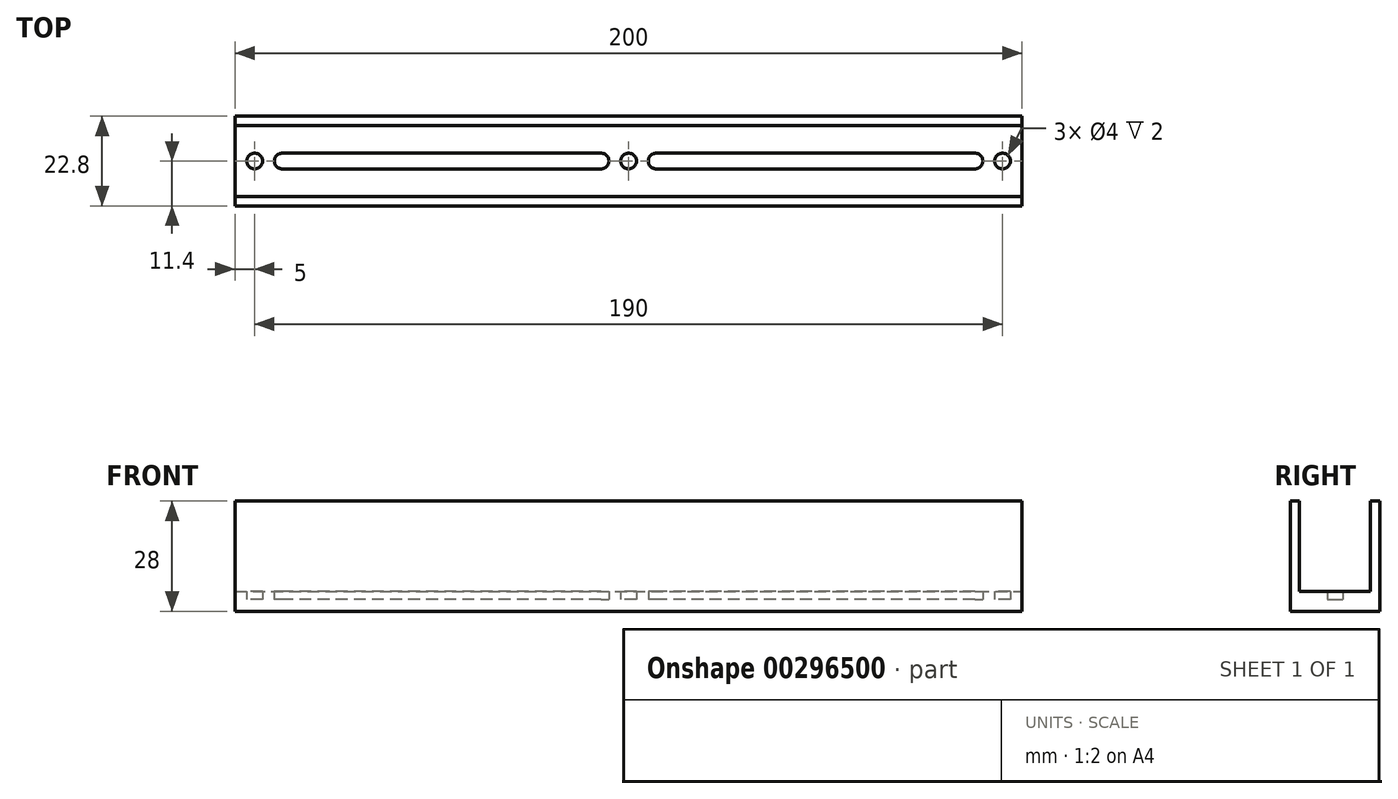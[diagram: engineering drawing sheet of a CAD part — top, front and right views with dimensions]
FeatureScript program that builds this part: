
annotation { "Feature Type Name" : "Feature", "Feature Type Description" : "" }
export const myFeature = defineFeature(function(context is Context, id is Id, definition is map)
    precondition{}
    {
        {
            var Q0;
            Q0=qCreatedBy(makeId("Top.planeOp"),FACE);
            var sketch = newSketch(context, id + "F0", { "sketchPlane" : qUnion([Q0])});
            skLineSegment(sketch, "E0.bottom", {"start": v(0, 0) * mm, "end": v(200, 0) * mm});
            skLineSegment(sketch, "E0.top", {"start": v(0, 18) * mm, "end": v(200, 18) * mm});
            skLineSegment(sketch, "E0.left", {"start": v(0, 0) * mm, "end": v(0, 18) * mm});
            skLineSegment(sketch, "E0.right", {"start": v(200, 0) * mm, "end": v(200, 18) * mm});
            skLineSegment(sketch, "E1", {"start": v(200, 9) * mm, "end": v(0, 9) * mm, "construction": true});
            skCircle(sketch, "E2", {"center": v(100, 9) * mm, "radius": 2 * mm});
            skCircle(sketch, "E3", {"center": v(5, 9) * mm, "radius": 2 * mm});
            skArc(sketch, "E4", {"start": v(93, 11) * mm, "mid": v(95, 9) * mm, "end": v(93, 7) * mm});
            skPoint(sketch, "E5", {"position": v(95, 9) * mm});
            skPoint(sketch, "E6", {"position": v(98, 9) * mm});
            skArc(sketch, "E7", {"start": v(12, 11) * mm, "mid": v(10, 9) * mm, "end": v(12, 7) * mm});
            skLineSegment(sketch, "E8", {"start": v(93, 11) * mm, "end": v(12, 11) * mm});
            skLineSegment(sketch, "E9", {"start": v(12, 7) * mm, "end": v(93, 7) * mm});
            skPoint(sketch, "E10", {"position": v(10, 9) * mm});
            skLineSegment(sketch, "E11", {"start": v(100, 18) * mm, "end": v(100, 0) * mm, "construction": true});
            skPoint(sketch, "E12.MirrorP", {"position": v(102, 9) * mm});
            skArc(sketch, "E13.MirrorCS", {"start": v(188, 11) * mm, "mid": v(190, 9) * mm, "end": v(188, 7) * mm});
            skArc(sketch, "E14.MirrorCS", {"start": v(107, 11) * mm, "mid": v(105, 9) * mm, "end": v(107, 7) * mm});
            skPoint(sketch, "E15.MirrorP", {"position": v(105, 9) * mm});
            skPoint(sketch, "E16.MirrorP", {"position": v(190, 9) * mm});
            skLineSegment(sketch, "E17.MirrorCS", {"start": v(188, 7) * mm, "end": v(107, 7) * mm});
            skLineSegment(sketch, "E18.MirrorCS", {"start": v(107, 11) * mm, "end": v(188, 11) * mm});
            skLineSegment(sketch, "E19.MirrorCS", {"start": v(0, 9) * mm, "end": v(200, 9) * mm, "construction": true});
            skCircle(sketch, "E20.MirrorC", {"center": v(195, 9) * mm, "radius": 2 * mm});
            skSolve(sketch);
        }
        {
            var Q0;
            Q0 = qSketchRegion(id + "F0", true);
            extrude(context, id + "F1", {"entities" : qUnion([Q0]), "depth" : 2 * mm});
        }
        {
            var Q0;
            Q0=makeQuery(id+"F1.opExtrude","CAP_FACE",FACE,{"disambiguationData":[OSD([sQuery(id+"F0.wireOp",EDGE,"E0.bottom"),sQuery(id+"F0.wireOp",EDGE,"E0.top"),sQuery(id+"F0.wireOp",EDGE,"E0.left"),sQuery(id+"F0.wireOp",EDGE,"E0.right"),sQuery(id+"F0.wireOp",EDGE,"E2"),sQuery(id+"F0.wireOp",EDGE,"E3"),sQuery(id+"F0.wireOp",EDGE,"E4"),sQuery(id+"F0.wireOp",EDGE,"E7"),sQuery(id+"F0.wireOp",EDGE,"E8"),sQuery(id+"F0.wireOp",EDGE,"E9"),sQuery(id+"F0.wireOp",EDGE,"E13.MirrorCS"),sQuery(id+"F0.wireOp",EDGE,"E14.MirrorCS"),sQuery(id+"F0.wireOp",EDGE,"E17.MirrorCS"),sQuery(id+"F0.wireOp",EDGE,"E18.MirrorCS"),sQuery(id+"F0.wireOp",EDGE,"E20.MirrorC")])],"isStart":true});
            var sketch = newSketch(context, id + "F2", { "sketchPlane" : qUnion([Q0])});
            skLineSegment(sketch, "E21.bottom", {"start": v(0, 0) * mm, "end": v(200, 0) * mm});
            skLineSegment(sketch, "E21.top", {"start": v(0, 2.4) * mm, "end": v(200, 2.4) * mm});
            skLineSegment(sketch, "E21.left", {"start": v(0, 0) * mm, "end": v(0, 2.4) * mm});
            skLineSegment(sketch, "E21.right", {"start": v(200, 0) * mm, "end": v(200, 2.4) * mm});
            skLineSegment(sketch, "E22.bottom", {"start": v(0, -18) * mm, "end": v(200, -18) * mm});
            skLineSegment(sketch, "E22.top", {"start": v(0, -20.4) * mm, "end": v(200, -20.4) * mm});
            skLineSegment(sketch, "E22.left", {"start": v(0, -18) * mm, "end": v(0, -20.4) * mm});
            skLineSegment(sketch, "E22.right", {"start": v(200, -18) * mm, "end": v(200, -20.4) * mm});
            skSolve(sketch);
        }
        {
            var Q0;
            Q0 = qSketchRegion(id + "F2", true);
            extrude(context, id + "F3", {"entities" : qUnion([Q0]), "operationType" : NewBodyOperationType.ADD, "oppositeDirection" : true, "depth" : 25 * mm});
        }
        {
            var Q0;
            Q0=makeQuery(id+"F3.boolean.opBoolean","MERGE",FACE,{"derivedFrom":[makeQuery(id+"F1.opExtrude","CAP_FACE",FACE,{"disambiguationData":[OSD([sQuery(id+"F0.wireOp",EDGE,"E0.bottom"),sQuery(id+"F0.wireOp",EDGE,"E0.top"),sQuery(id+"F0.wireOp",EDGE,"E0.left"),sQuery(id+"F0.wireOp",EDGE,"E0.right"),sQuery(id+"F0.wireOp",EDGE,"E2"),sQuery(id+"F0.wireOp",EDGE,"E3"),sQuery(id+"F0.wireOp",EDGE,"E4"),sQuery(id+"F0.wireOp",EDGE,"E7"),sQuery(id+"F0.wireOp",EDGE,"E8"),sQuery(id+"F0.wireOp",EDGE,"E9"),sQuery(id+"F0.wireOp",EDGE,"E13.MirrorCS"),sQuery(id+"F0.wireOp",EDGE,"E14.MirrorCS"),sQuery(id+"F0.wireOp",EDGE,"E17.MirrorCS"),sQuery(id+"F0.wireOp",EDGE,"E18.MirrorCS"),sQuery(id+"F0.wireOp",EDGE,"E20.MirrorC")])],"isStart":true}),makeQuery(id+"F3.opExtrude","CAP_FACE",FACE,{"disambiguationData":[OSD([sQuery(id+"F2.wireOp",EDGE,"E21.bottom"),sQuery(id+"F2.wireOp",EDGE,"E21.top"),sQuery(id+"F2.wireOp",EDGE,"E21.left"),sQuery(id+"F2.wireOp",EDGE,"E21.right")])],"isStart":true}),makeQuery(id+"F3.opExtrude","CAP_FACE",FACE,{"disambiguationData":[OSD([sQuery(id+"F2.wireOp",EDGE,"E22.bottom"),sQuery(id+"F2.wireOp",EDGE,"E22.top"),sQuery(id+"F2.wireOp",EDGE,"E22.left"),sQuery(id+"F2.wireOp",EDGE,"E22.right")])],"isStart":true})]});
            var sketch = newSketch(context, id + "F4", { "sketchPlane" : qUnion([Q0])});
            skLineSegment(sketch, "E23.bottom", {"start": v(200, -20.4) * mm, "end": v(0, -20.4) * mm});
            skLineSegment(sketch, "E23.top", {"start": v(200, 2.4) * mm, "end": v(0, 2.4) * mm});
            skLineSegment(sketch, "E23.left", {"start": v(200, -20.4) * mm, "end": v(200, 2.4) * mm});
            skLineSegment(sketch, "E23.right", {"start": v(0, -20.4) * mm, "end": v(0, 2.4) * mm});
            skSolve(sketch);
        }
        {
            var Q0;
            Q0 = qSketchRegion(id + "F4", true);
            extrude(context, id + "F5", {"entities" : qUnion([Q0]), "operationType" : NewBodyOperationType.ADD, "depth" : 3 * mm});
        }
    });
